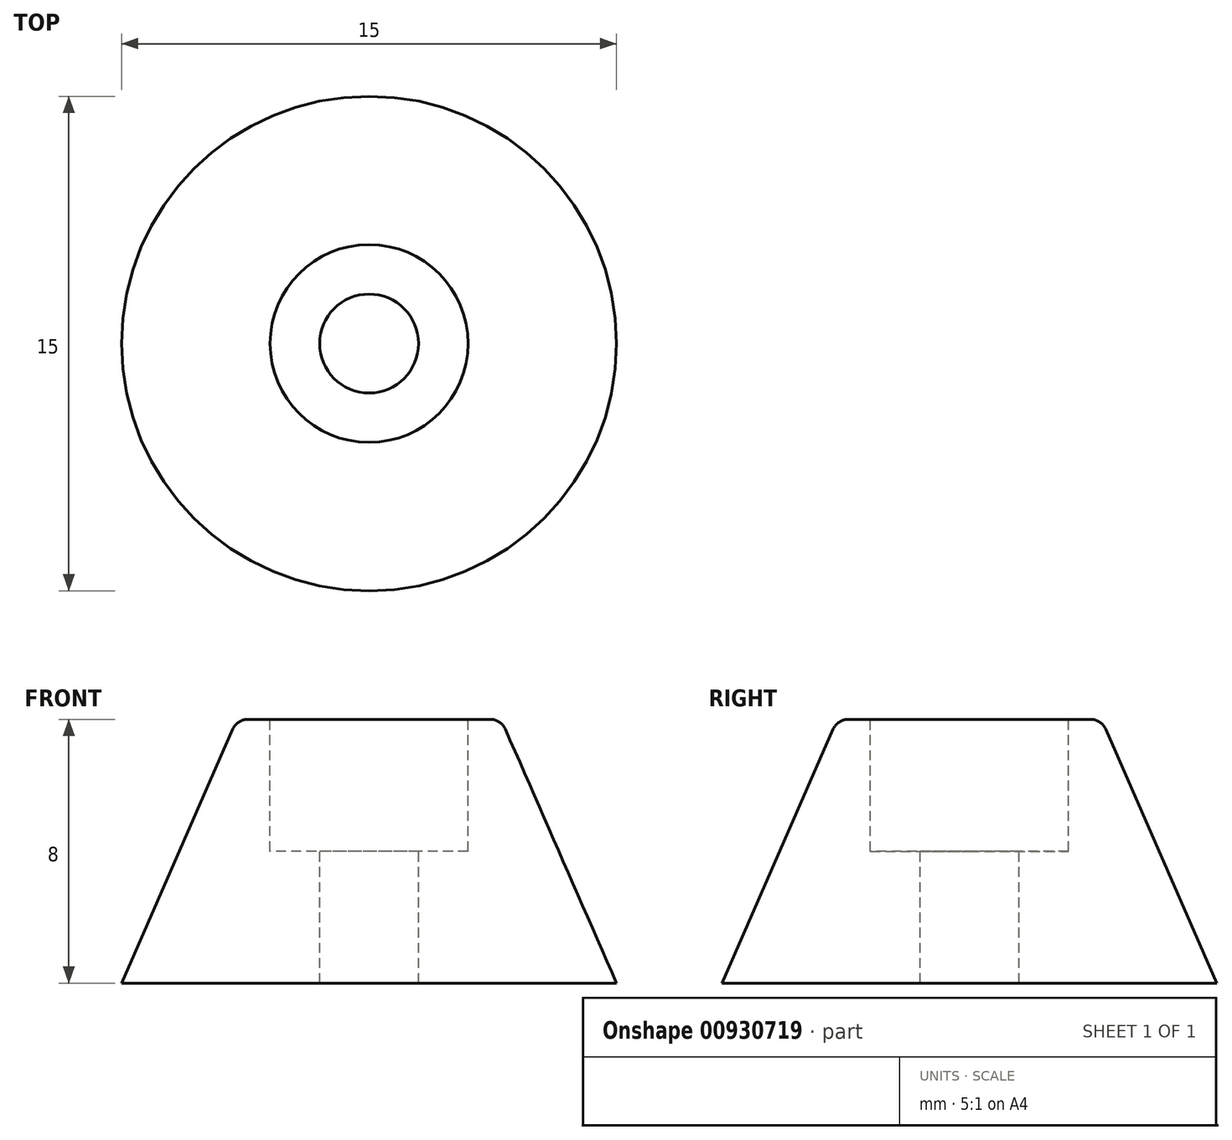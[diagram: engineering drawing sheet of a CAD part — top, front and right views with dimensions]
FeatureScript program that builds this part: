
annotation { "Feature Type Name" : "Feature", "Feature Type Description" : "" }
export const myFeature = defineFeature(function(context is Context, id is Id, definition is map)
    precondition{}
    {
        {
            var Q0;
            Q0=qCreatedBy(makeId("Top.planeOp"),FACE);
            var sketch = newSketch(context, id + "F0", { "sketchPlane" : qUnion([Q0])});
            skCircle(sketch, "E0", {"center": v(0, 0) * mm, "radius": 7.5 * mm});
            skSolve(sketch);
        }
        {
            var Q0;
            Q0=qCreatedBy(makeId("Front.planeOp"),FACE);
            var sketch = newSketch(context, id + "F1", { "sketchPlane" : qUnion([Q0])});
            skLineSegment(sketch, "E1", {"start": v(0, 0) * mm, "end": v(0, 4) * mm});
            skLineSegment(sketch, "E2", {"start": v(0, 4) * mm, "end": v(0, 8) * mm});
            skLineSegment(sketch, "E3", {"start": v(0, 0) * mm, "end": v(7.5, 0) * mm});
            skLineSegment(sketch, "E4", {"start": v(0, 8) * mm, "end": v(4, 8) * mm});
            skLineSegment(sketch, "E5", {"start": v(4, 8) * mm, "end": v(7.5, 0) * mm});
            skSolve(sketch);
        }
        {
            var Q0;
            Q0=makeQuery(id+"F1.imprint","IMPRINT",FACE,{"disambiguationData":[TD([[makeQuery(id+"F1.imprint","IMPRINT",EDGE,{"derivedFrom":sQuery(id+"F1.wireOp",EDGE,"E1")}),-1.0]])]});
            var Q1;
            Q1=sQuery(id+"F0.wireOp",EDGE,"E0");
            sweep(context, id + "F2", {"profiles" : qUnion([Q0]), "path" : qUnion([Q1])});
        }
        {
            var Q0;
            Q0=makeQuery(id+"F2.opSweep","SWEPT_FACE",FACE,{"disambiguationData":[OSD([sQuery(id+"F0.wireOp",EDGE,"E0"),sQuery(id+"F1.wireOp",EDGE,"E4")])]});
            var sketch = newSketch(context, id + "F3", { "sketchPlane" : qUnion([Q0])});
            skCircle(sketch, "E6", {"center": v(0, 0) * mm, "radius": 3 * mm});
            skSolve(sketch);
        }
        {
            var Q0;
            Q0 = qSketchRegion(id + "F3", true);
            extrude(context, id + "F4", {"entities" : qUnion([Q0]), "operationType" : NewBodyOperationType.REMOVE, "oppositeDirection" : true, "depth" : 4 * mm, "offsetDistance" : 25 * mm});
        }
        {
            var Q0;
            Q0=makeQuery(id+"F4.boolean.opBoolean","COPY",FACE,{"derivedFrom":makeQuery(id+"F4.opExtrude","CAP_FACE",FACE,{"disambiguationData":[OSD([sQuery(id+"F3.wireOp",EDGE,"E6")])],"isStart":false})});
            var sketch = newSketch(context, id + "F5", { "sketchPlane" : qUnion([Q0])});
            skCircle(sketch, "E7", {"center": v(0, 0) * mm, "radius": 1.5 * mm});
            skSolve(sketch);
        }
        {
            var Q0;
            Q0 = qSketchRegion(id + "F5", true);
            extrude(context, id + "F6", {"entities" : qUnion([Q0]), "operationType" : NewBodyOperationType.REMOVE, "endBound" : BoundingType.THROUGH_ALL, "oppositeDirection" : true, "depth" : 25 * mm, "offsetDistance" : 25 * mm});
        }
        {
            var Q0;
            Q0=makeQuery(id+"F2.opSweep","SWEPT_EDGE",EDGE,{"disambiguationData":[OSD([sQuery(id+"F0.wireOp",EDGE,"E0"),sQuery(id+"F1.wireOp",EDGE,"E4"),sQuery(id+"F1.wireOp",EDGE,"E5")])]});
            fillet(context, id + "F7", {"entities" : qUnion([Q0]), "radius" : 0.5 * mm, "tangentPropagation" : true, "allowEdgeOverflow" : false});
        }
    });
